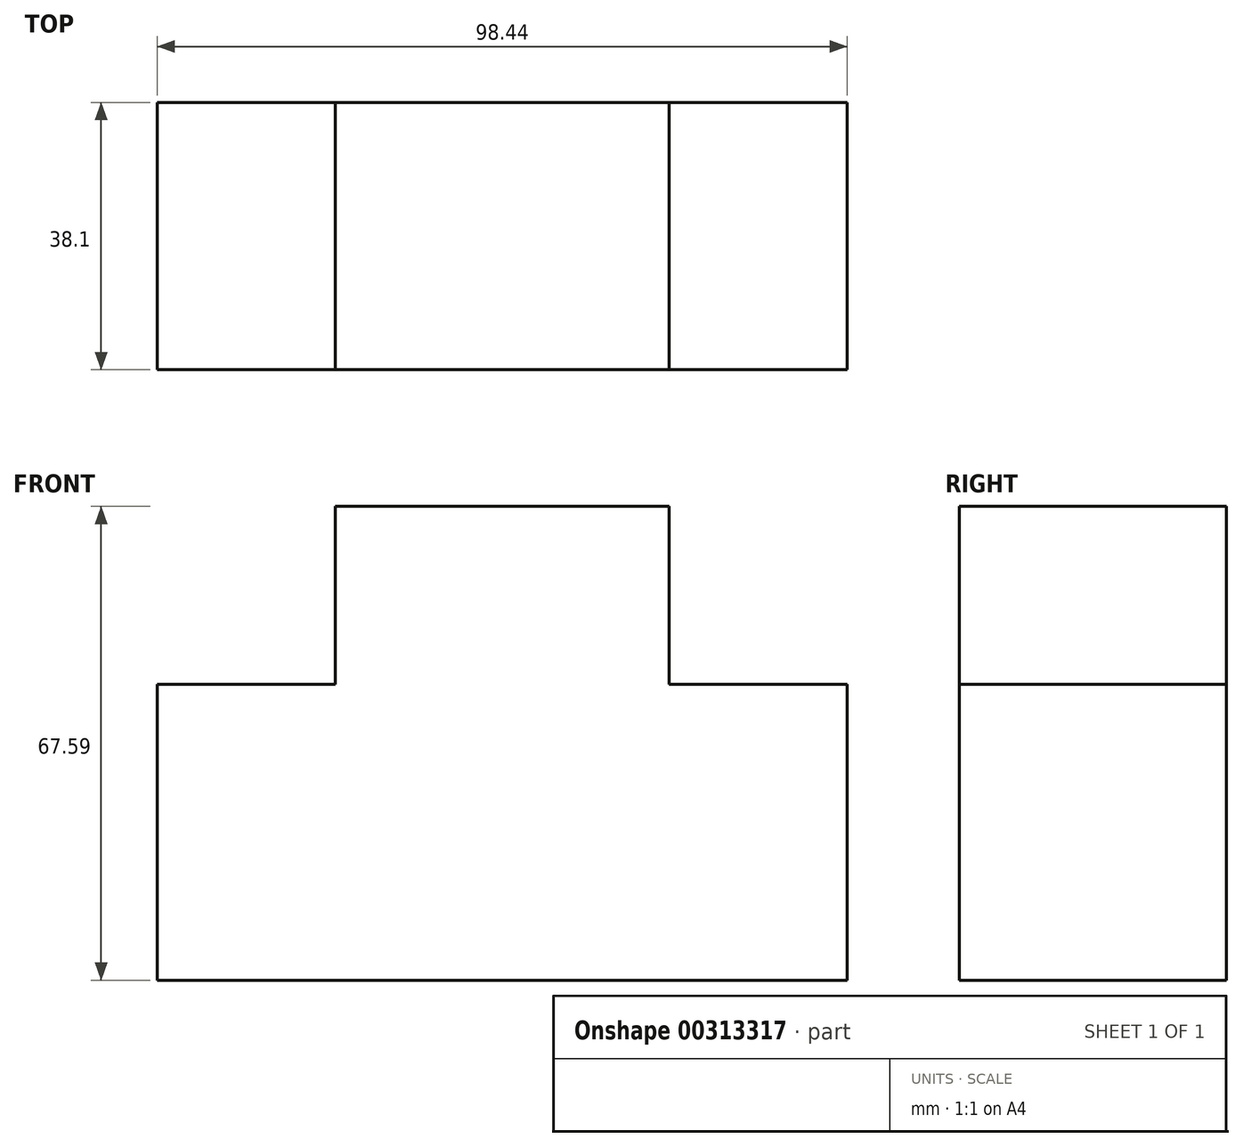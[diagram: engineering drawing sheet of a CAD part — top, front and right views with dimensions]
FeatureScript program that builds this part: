
annotation { "Feature Type Name" : "Feature", "Feature Type Description" : "" }
export const myFeature = defineFeature(function(context is Context, id is Id, definition is map)
    precondition{}
    {
        {
            var Q0;
            Q0=qCreatedBy(makeId("Front.planeOp"),FACE);
            var sketch = newSketch(context, id + "F0", { "sketchPlane" : qUnion([Q0])});
            skLineSegment(sketch, "E0", {"start": v(-53.09, -18.91) * mm, "end": v(45.35, -18.91) * mm});
            skLineSegment(sketch, "E1", {"start": v(-53.09, -18.91) * mm, "end": v(-53.09, 23.28) * mm});
            skLineSegment(sketch, "E2", {"start": v(45.35, -18.91) * mm, "end": v(45.35, 23.28) * mm});
            skLineSegment(sketch, "E3", {"start": v(-53.09, 23.28) * mm, "end": v(-27.69, 23.28) * mm});
            skLineSegment(sketch, "E4", {"start": v(45.35, 23.28) * mm, "end": v(19.95, 23.28) * mm});
            skLineSegment(sketch, "E5", {"start": v(-27.69, 23.28) * mm, "end": v(-27.69, 48.68) * mm});
            skLineSegment(sketch, "E6", {"start": v(19.95, 23.28) * mm, "end": v(19.95, 48.68) * mm});
            skLineSegment(sketch, "E7", {"start": v(-27.69, 48.68) * mm, "end": v(19.95, 48.68) * mm});
            skSolve(sketch);
        }
        {
            var Q0;
            Q0=makeQuery(id+"F0.imprint","IMPRINT",FACE,{"disambiguationData":[TD([[makeQuery(id+"F0.imprint","IMPRINT",EDGE,{"derivedFrom":sQuery(id+"F0.wireOp",EDGE,"E0")}),1.0]])]});
            extrude(context, id + "F1", {"entities" : qUnion([Q0]), "depth" : 38.1 * mm});
        }
    });
